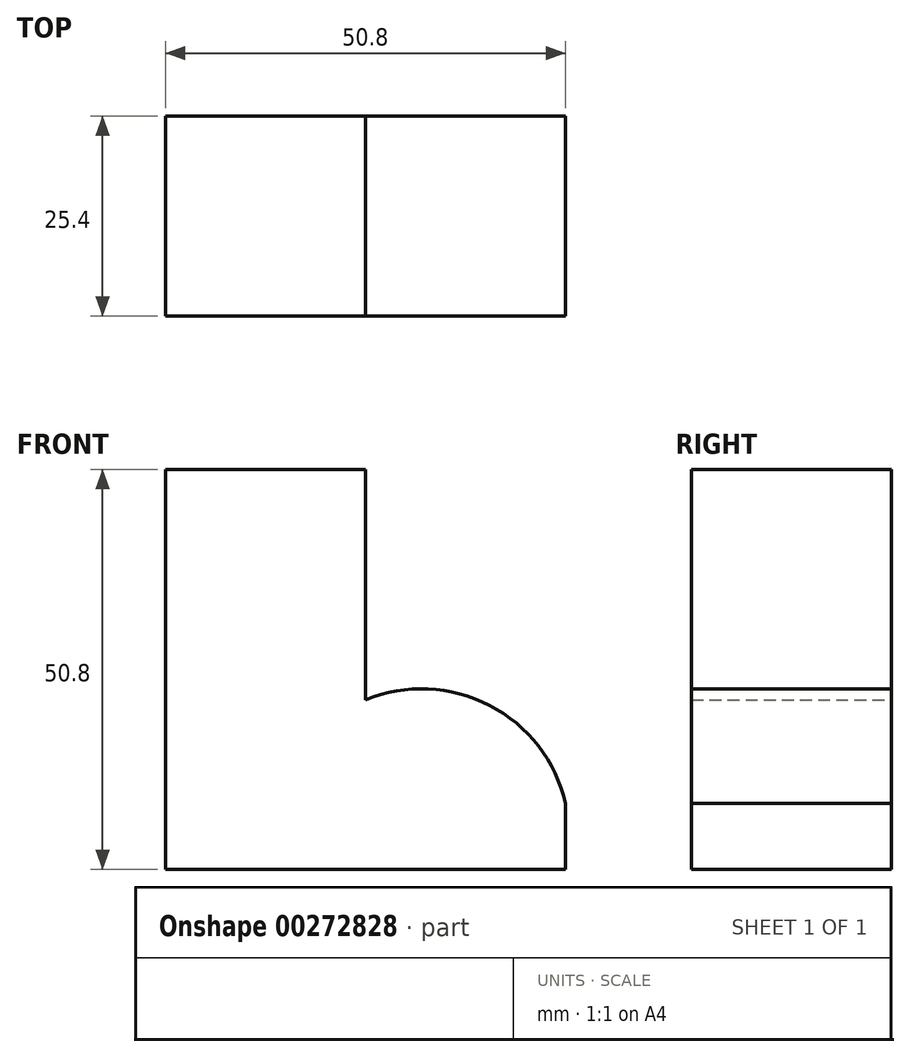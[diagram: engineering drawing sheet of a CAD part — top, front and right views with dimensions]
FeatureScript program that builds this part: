
annotation { "Feature Type Name" : "Feature", "Feature Type Description" : "" }
export const myFeature = defineFeature(function(context is Context, id is Id, definition is map)
    precondition{}
    {
        {
            var Q0;
            Q0=qCreatedBy(makeId("Front.planeOp"),FACE);
            var sketch = newSketch(context, id + "F0", { "sketchPlane" : qUnion([Q0])});
            skLineSegment(sketch, "E0", {"start": v(0, 0) * mm, "end": v(-50.8, 0) * mm});
            skLineSegment(sketch, "E1", {"start": v(-50.8, 0) * mm, "end": v(-50.8, 50.8) * mm});
            skLineSegment(sketch, "E2", {"start": v(-50.8, 50.8) * mm, "end": v(-25.4, 50.8) * mm});
            skLineSegment(sketch, "E3", {"start": v(-25.4, 50.8) * mm, "end": v(-25.4, 25.4) * mm});
            skLineSegment(sketch, "E4", {"start": v(-25.4, 25.4) * mm, "end": v(-25.4, 21.53) * mm});
            skLineSegment(sketch, "E5", {"start": v(0, 0) * mm, "end": v(0, 21.53) * mm});
            skLineSegment(sketch, "E6", {"start": v(-11.14, 21.53) * mm, "end": v(-25.4, 21.53) * mm});
            skPoint(sketch, "E7.orphan", {"position": v(-25.4, 0) * mm});
            skArc(sketch, "E8", {"start": v(0, 0) * mm, "mid": v(-6.15, 18.5) * mm, "end": v(-25.4, 21.53) * mm});
            skSolve(sketch);
        }
        {
            var Q0;
            {var subQ4=sQuery(id+"F0.wireOp",EDGE,"E0");Q0=makeQuery(id+"F0.imprint","IMPRINT",FACE,{"disambiguationData":[TD([[makeQuery(id+"F0.imprint","IMPRINT",EDGE,{"derivedFrom":subQ4}),-1.0]])]});}
            extrude(context, id + "F1", {"entities" : qUnion([Q0]), "depth" : 25.4 * mm});
        }
        {
            var Q0;
            {var subQ0=sQuery(id+"F0.wireOp",EDGE,"E6");Q0=makeQuery(id+"F0.imprint","IMPRINT",FACE,{"disambiguationData":[TD([[makeQuery(id+"F0.imprint","IMPRINT",EDGE,{"derivedFrom":subQ0}),-1.0]])]});}
            extrude(context, id + "F2", {"entities" : qUnion([Q0]), "operationType" : NewBodyOperationType.ADD, "depth" : 25.4 * mm});
        }
    });
